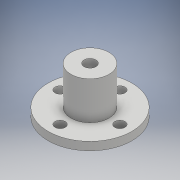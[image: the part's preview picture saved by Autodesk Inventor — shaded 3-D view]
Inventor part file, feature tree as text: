
AUTODESK INVENTOR PART (.ipt)
format: ipt  version: 2018 (Build 220112000, 112)  size: 124,416 bytes
history: native  units: mm
features: extrude x4, sketch x4, other x1, pattern_circular x1
ambient origin geometry x8: Origin, YZ Plane, XZ Plane, XY Plane, X Axis, Y Axis, Z Axis, Center Point
bodies: Body1 (feature_tree)
feature tree (10):
  other  "ソリッド1"
  extrude  "押し出し1"  Depth=22.0mm
  extrude  "押し出し2"  Depth=2.16mm TaperAngle=0.0deg
  extrude  "押し出し3"  Depth=10.0mm
  extrude  "押し出し4"  Depth=10.0mm TaperAngle=0.0deg
  pattern_circular  "円形状パターン1"  [2 undecoded]
  sketch  "スケッチ1"
  sketch  "スケッチ2"
  sketch  "スケッチ3"
  sketch  "スケッチ4"
note: 2 required parameter values undecoded (feature->parameter linkage not recoverable at this tier; creation-order binding heuristic only, values carry confidence <= 0.55)
